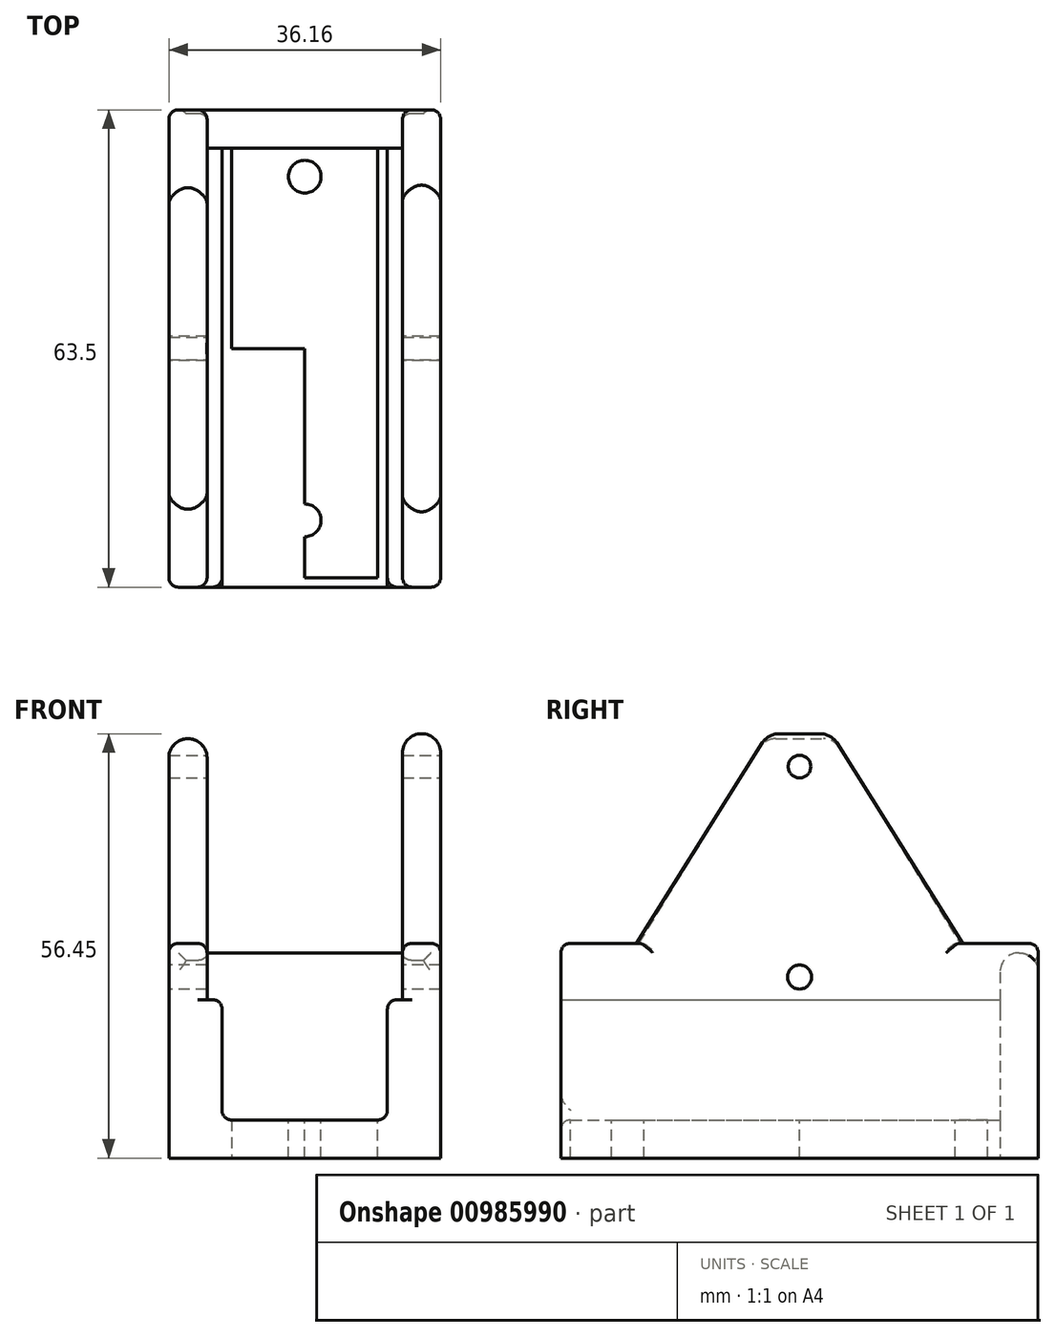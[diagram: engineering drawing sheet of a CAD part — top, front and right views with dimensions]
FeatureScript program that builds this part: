
annotation { "Feature Type Name" : "Feature", "Feature Type Description" : "" }
export const myFeature = defineFeature(function(context is Context, id is Id, definition is map)
    precondition{}
    {
        {
            var Q0;
            Q0=qCreatedBy(makeId("Front.planeOp"),FACE);
            var sketch = newSketch(context, id + "F0", { "sketchPlane" : qUnion([Q0])});
            skLineSegment(sketch, "E0", {"start": v(0, 0) * mm, "end": v(0, 23.5) * mm});
            skLineSegment(sketch, "E1", {"start": v(0, 0) * mm, "end": v(26, 0) * mm});
            skLineSegment(sketch, "E2", {"start": v(26, 0) * mm, "end": v(26, 23.5) * mm});
            skLineSegment(sketch, "E3.0", {"start": v(31.08, -5.08) * mm, "end": v(31.08, 23.5) * mm});
            skLineSegment(sketch, "E3.1", {"start": v(-5.08, -5.08) * mm, "end": v(31.08, -5.08) * mm});
            skLineSegment(sketch, "E3.2", {"start": v(-5.08, -5.08) * mm, "end": v(-5.08, 23.5) * mm});
            skLineSegment(sketch, "E4", {"start": v(-5.08, 23.5) * mm, "end": v(0, 23.5) * mm});
            skLineSegment(sketch, "E5", {"start": v(26, 23.5) * mm, "end": v(31.08, 23.5) * mm});
            skPoint(sketch, "E6.visualSharp", {"position": v(26, 0) * mm});
            skLineSegment(sketch, "E6.filletArc", {"start": v(26, 0) * mm, "end": v(26, 0) * mm});
            skPoint(sketch, "E7.visualSharp", {"position": v(0, 0) * mm});
            skLineSegment(sketch, "E7.filletArc", {"start": v(0, 0) * mm, "end": v(0, 0) * mm});
            skLineSegment(sketch, "E8.bottom", {"start": v(0, 0) * mm, "end": v(2, 0) * mm});
            skLineSegment(sketch, "E8.top", {"start": v(0, 16) * mm, "end": v(2, 16) * mm});
            skLineSegment(sketch, "E8.left", {"start": v(0, 0) * mm, "end": v(0, 16) * mm});
            skLineSegment(sketch, "E8.right", {"start": v(2, 0) * mm, "end": v(2, 16) * mm});
            skLineSegment(sketch, "E9.MirrorCS", {"start": v(24, 0) * mm, "end": v(24, 16) * mm});
            skLineSegment(sketch, "E10.MirrorCS", {"start": v(26, 16) * mm, "end": v(24, 16) * mm});
            skLineSegment(sketch, "E11.MirrorCS", {"start": v(26, 0) * mm, "end": v(26, 16) * mm});
            skLineSegment(sketch, "E12.MirrorCS", {"start": v(26, 0) * mm, "end": v(24, 0) * mm});
            skLineSegment(sketch, "E13", {"start": v(24, 0) * mm, "end": v(30.18, 0) * mm});
            skPoint(sketch, "E13.endSnap0", {"position": v(25, 0) * mm});
            skSolve(sketch);
        }
        {
            var Q0;
            Q0 = qSketchRegion(id + "F0", true);
            var Q1;
            Q1=sQuery(id+"F0.wireOp",EDGE,"E1");
            extrude(context, id + "F1", {"entities" : qUnion([Q0]), "surfaceEntities" : qUnion([Q1]), "endBound" : BoundingType.SYMMETRIC, "depth" : 63.5 * mm, "offsetDistance" : 25.4 * mm});
        }
        {
            var Q0;
            Q0=makeQuery(id+"F1.opExtrude","SWEPT_FACE",FACE,{"disambiguationData":[OSD([sQuery(id+"F0.wireOp",EDGE,"E3.2")])]});
            var sketch = newSketch(context, id + "F2", { "sketchPlane" : qUnion([Q0])});
            skCircle(sketch, "E14", {"center": v(0, 19) * mm, "radius": 1.6 * mm});
            skLineSegment(sketch, "E15", {"start": v(0, 0) * mm, "end": v(0, 23.5) * mm, "construction": true});
            skLineSegment(sketch, "E16", {"start": v(-31.75, 19) * mm, "end": v(31.75, 19) * mm, "construction": true});
            skLineSegment(sketch, "E17", {"start": v(31.75, 0) * mm, "end": v(-31.75, 0) * mm, "construction": true});
            skLineSegment(sketch, "E18", {"start": v(0, 12.26) * mm, "end": v(-31.75, 12.26) * mm, "construction": true});
            skLineSegment(sketch, "E19", {"start": v(0, 8.67) * mm, "end": v(31.75, 8.67) * mm, "construction": true});
            skLineSegment(sketch, "E20", {"start": v(-6.34, 0) * mm, "end": v(-6.34, 19) * mm, "construction": true});
            skSolve(sketch);
        }
        {
            var Q0;
            Q0 = qSketchRegion(id + "F2", true);
            extrude(context, id + "F3", {"entities" : qUnion([Q0]), "operationType" : NewBodyOperationType.REMOVE, "endBound" : BoundingType.THROUGH_ALL, "oppositeDirection" : true, "depth" : 25.4 * mm, "offsetDistance" : 25.4 * mm});
        }
        {
            var Q0;
            Q0=makeQuery(id+"F1.opExtrude","SWEPT_EDGE",EDGE,{"disambiguationData":[OSD([sQuery(id+"F0.wireOp",EDGE,"E9.MirrorCS"),sQuery(id+"F0.wireOp",EDGE,"E10.MirrorCS")])]});
            var Q1;
            Q1=makeQuery(id+"F1.opExtrude","SWEPT_EDGE",EDGE,{"disambiguationData":[OSD([sQuery(id+"F0.wireOp",EDGE,"E8.top"),sQuery(id+"F0.wireOp",EDGE,"E8.right")])]});
            var Q2;
            Q2=makeQuery(id+"F1.opExtrude","SWEPT_EDGE",EDGE,{"disambiguationData":[OSD([sQuery(id+"F0.wireOp",EDGE,"E2"),sQuery(id+"F0.wireOp",EDGE,"E5")])]});
            var Q3;
            Q3=makeQuery(id+"F1.opExtrude","SWEPT_EDGE",EDGE,{"disambiguationData":[OSD([sQuery(id+"F0.wireOp",EDGE,"E3.0"),sQuery(id+"F0.wireOp",EDGE,"E5")])]});
            var Q4;
            Q4=makeQuery(id+"F1.opExtrude","SWEPT_EDGE",EDGE,{"disambiguationData":[OSD([sQuery(id+"F0.wireOp",EDGE,"E0"),sQuery(id+"F0.wireOp",EDGE,"E4")])]});
            var Q5;
            Q5=makeQuery(id+"F1.opExtrude","SWEPT_EDGE",EDGE,{"disambiguationData":[OSD([sQuery(id+"F0.wireOp",EDGE,"E3.2"),sQuery(id+"F0.wireOp",EDGE,"E4")])]});
            var Q6;
            Q6=makeQuery(id+"F1.opExtrude","SWEPT_EDGE",EDGE,{"disambiguationData":[OSD([sQuery(id+"F0.wireOp",EDGE,"E1"),sQuery(id+"F0.wireOp",EDGE,"E9.MirrorCS"),sQuery(id+"F0.wireOp",EDGE,"E13")])]});
            var Q7;
            Q7=makeQuery(id+"F1.opExtrude","SWEPT_EDGE",EDGE,{"disambiguationData":[OSD([sQuery(id+"F0.wireOp",EDGE,"E1"),sQuery(id+"F0.wireOp",EDGE,"E8.bottom"),sQuery(id+"F0.wireOp",EDGE,"E8.right")])]});
            var Q8;
            Q8=makeQuery(id+"F1.opExtrude","CAP_EDGE",EDGE,{"disambiguationData":[OSD([sQuery(id+"F0.wireOp",EDGE,"E1")])],"isStart":true});
            var Q9;
            Q9=makeQuery(id+"F1.opExtrude","CAP_EDGE",EDGE,{"disambiguationData":[OSD([sQuery(id+"F0.wireOp",EDGE,"E1")])],"isStart":false});
            var Q10;
            Q10=makeQuery(id+"F1.opExtrude","CAP_EDGE",EDGE,{"disambiguationData":[OSD([sQuery(id+"F0.wireOp",EDGE,"E0")])],"isStart":false});
            var Q11;
            Q11=makeQuery(id+"F1.opExtrude","CAP_EDGE",EDGE,{"disambiguationData":[OSD([sQuery(id+"F0.wireOp",EDGE,"E2")])],"isStart":false});
            var Q12;
            Q12=makeQuery(id+"F1.opExtrude","CAP_EDGE",EDGE,{"disambiguationData":[OSD([sQuery(id+"F0.wireOp",EDGE,"E2")])],"isStart":true});
            var Q13;
            Q13=makeQuery(id+"F1.opExtrude","CAP_EDGE",EDGE,{"disambiguationData":[OSD([sQuery(id+"F0.wireOp",EDGE,"E0")])],"isStart":true});
            var Q14;
            Q14=makeQuery(id+"F1.opExtrude","CAP_EDGE",EDGE,{"disambiguationData":[OSD([sQuery(id+"F0.wireOp",EDGE,"E3.0")])],"isStart":true});
            var Q15;
            Q15=makeQuery(id+"F1.opExtrude","CAP_EDGE",EDGE,{"disambiguationData":[OSD([sQuery(id+"F0.wireOp",EDGE,"E3.2")])],"isStart":true});
            var Q16;
            Q16=makeQuery(id+"F1.opExtrude","CAP_EDGE",EDGE,{"disambiguationData":[OSD([sQuery(id+"F0.wireOp",EDGE,"E3.2")])],"isStart":false});
            var Q17;
            Q17=makeQuery(id+"F1.opExtrude","CAP_EDGE",EDGE,{"disambiguationData":[OSD([sQuery(id+"F0.wireOp",EDGE,"E3.0")])],"isStart":false});
            var Q18;
            Q18=makeQuery(id+"F1.opExtrude","CAP_EDGE",EDGE,{"disambiguationData":[OSD([sQuery(id+"F0.wireOp",EDGE,"E4")])],"isStart":false});
            var Q19;
            Q19=makeQuery(id+"F1.opExtrude","CAP_EDGE",EDGE,{"disambiguationData":[OSD([sQuery(id+"F0.wireOp",EDGE,"E5")])],"isStart":false});
            var Q20;
            Q20=makeQuery(id+"F1.opExtrude","CAP_EDGE",EDGE,{"disambiguationData":[OSD([sQuery(id+"F0.wireOp",EDGE,"E4")])],"isStart":true});
            var Q21;
            Q21=makeQuery(id+"F1.opExtrude","CAP_EDGE",EDGE,{"disambiguationData":[OSD([sQuery(id+"F0.wireOp",EDGE,"E5")])],"isStart":true});
            fillet(context, id + "F4", {"entities" : qUnion([Q0, Q1, Q2, Q3, Q4, Q5, Q6, Q7, Q8, Q9, Q10, Q11, Q12, Q13, Q14, Q15, Q16, Q17, Q18, Q19, Q20, Q21]), "tangentPropagation" : true, "radius" : 1.27 * mm, "defaultsChanged" : false, "vertexSettings" : [], "allowEdgeOverflow" : false});
        }
        {
            var Q0;
            Q0=makeQuery(id+"F1.opExtrude","SWEPT_FACE",FACE,{"disambiguationData":[OSD([sQuery(id+"F0.wireOp",EDGE,"E3.0")])]});
            var sketch = newSketch(context, id + "F5", { "sketchPlane" : qUnion([Q0])});
            skLineSegment(sketch, "E21", {"start": v(-22.52, 22.23) * mm, "end": v(-4.93, 50.18) * mm});
            skLineSegment(sketch, "E22.MirrorCS", {"start": v(22.52, 22.23) * mm, "end": v(4.93, 50.18) * mm});
            skLineSegment(sketch, "E23", {"start": v(-2.78, 51.37) * mm, "end": v(2.78, 51.37) * mm});
            skLineSegment(sketch, "E24", {"start": v(-22.52, 22.23) * mm, "end": v(22.52, 22.23) * mm});
            skPoint(sketch, "E25.visualSharp", {"position": v(-4.18, 51.37) * mm});
            skArc(sketch, "E25.filletArc", {"start": v(-2.78, 51.37) * mm, "mid": v(-4, 51.05) * mm, "end": v(-4.93, 50.18) * mm});
            skPoint(sketch, "E26.visualSharp", {"position": v(4.18, 51.37) * mm});
            skArc(sketch, "E26.filletArc", {"start": v(4.93, 50.18) * mm, "mid": v(4, 51.05) * mm, "end": v(2.78, 51.37) * mm});
            skSolve(sketch);
        }
        {
            var Q0;
            Q0=makeQuery(id+"F5.imprint","IMPRINT",FACE,{"disambiguationData":[TD([[makeQuery(id+"F5.imprint","IMPRINT",EDGE,{"derivedFrom":sQuery(id+"F5.wireOp",EDGE,"E21")}),-1.0]])]});
            extrude(context, id + "F6", {"entities" : qUnion([Q0]), "operationType" : NewBodyOperationType.ADD, "oppositeDirection" : true, "depth" : 5.08 * mm, "offsetDistance" : 25.4 * mm});
        }
        {
            var Q0;
            Q0=makeQuery(id+"F1.opExtrude","SWEPT_FACE",FACE,{"disambiguationData":[OSD([sQuery(id+"F0.wireOp",EDGE,"E3.2")])]});
            var sketch = newSketch(context, id + "F7", { "sketchPlane" : qUnion([Q0])});
            skLineSegment(sketch, "E27", {"start": v(-22.17, 22.22) * mm, "end": v(-4.57, 50.71) * mm});
            skLineSegment(sketch, "E28.MirrorCS", {"start": v(22.17, 22.22) * mm, "end": v(4.57, 50.71) * mm});
            skLineSegment(sketch, "E29", {"start": v(-4.57, 50.71) * mm, "end": v(4.57, 50.71) * mm});
            skLineSegment(sketch, "E30", {"start": v(-22.17, 22.23) * mm, "end": v(22.17, 22.22) * mm});
            skSolve(sketch);
        }
        {
            var Q0;
            Q0=makeQuery(id+"F7.imprint","IMPRINT",FACE,{"disambiguationData":[TD([[makeQuery(id+"F7.imprint","IMPRINT",EDGE,{"derivedFrom":sQuery(id+"F7.wireOp",EDGE,"E27")}),-1.0]])]});
            extrude(context, id + "F8", {"entities" : qUnion([Q0]), "operationType" : NewBodyOperationType.ADD, "oppositeDirection" : true, "depth" : 5.08 * mm, "offsetDistance" : 25.4 * mm});
        }
        {
            var Q0;
            Q0=makeQuery(id+"F8.opExtrude","SWEPT_EDGE",EDGE,{"disambiguationData":[OSD([sQuery(id+"F7.wireOp",EDGE,"E27"),sQuery(id+"F7.wireOp",EDGE,"E29")])]});
            var Q1;
            Q1=makeQuery(id+"F8.opExtrude","SWEPT_EDGE",EDGE,{"disambiguationData":[OSD([sQuery(id+"F7.wireOp",EDGE,"E28.MirrorCS"),sQuery(id+"F7.wireOp",EDGE,"E29")])]});
            var Q2;
            Q2=makeQuery(id+"F8.opExtrude","CAP_EDGE",EDGE,{"disambiguationData":[OSD([sQuery(id+"F7.wireOp",EDGE,"E28.MirrorCS")])],"isStart":false});
            var Q3;
            Q3=makeQuery(id+"F8.opExtrude","CAP_EDGE",EDGE,{"disambiguationData":[OSD([sQuery(id+"F7.wireOp",EDGE,"E28.MirrorCS")])],"isStart":true});
            var Q4;
            Q4=makeQuery(id+"F8.opExtrude","CAP_EDGE",EDGE,{"disambiguationData":[OSD([sQuery(id+"F7.wireOp",EDGE,"E27")])],"isStart":true});
            var Q5;
            Q5=makeQuery(id+"F8.opExtrude","CAP_EDGE",EDGE,{"disambiguationData":[OSD([sQuery(id+"F7.wireOp",EDGE,"E27")])],"isStart":false});
            var Q6;
            Q6=makeQuery(id+"F6.opExtrude","CAP_EDGE",EDGE,{"disambiguationData":[OSD([sQuery(id+"F5.wireOp",EDGE,"E22.MirrorCS")])],"isStart":false});
            var Q7;
            Q7=makeQuery(id+"F6.opExtrude","CAP_EDGE",EDGE,{"disambiguationData":[OSD([sQuery(id+"F5.wireOp",EDGE,"E22.MirrorCS")])],"isStart":true});
            var Q8;
            Q8=makeQuery(id+"F8.opExtrude","SWEPT_FACE",FACE,{"disambiguationData":[OSD([sQuery(id+"F7.wireOp",EDGE,"E29")])]});
            fillet(context, id + "F9", {"entities" : qUnion([Q0, Q1, Q2, Q3, Q4, Q5, Q6, Q7, Q8]), "tangentPropagation" : true, "radius" : 2.54 * mm, "defaultsChanged" : false, "vertexSettings" : [], "allowEdgeOverflow" : false});
        }
        {
            var Q0;
            Q0=makeQuery(id+"F1.opExtrude","SWEPT_FACE",FACE,{"disambiguationData":[OSD([sQuery(id+"F0.wireOp",EDGE,"E1")])]});
            var sketch = newSketch(context, id + "F10", { "sketchPlane" : qUnion([Q0])});
            skLineSegment(sketch, "E31", {"start": v(13, -30.48) * mm, "end": v(13, 30.48) * mm});
            skLineSegment(sketch, "E32", {"start": v(13, 0) * mm, "end": v(0, 0) * mm});
            skLineSegment(sketch, "E33", {"start": v(13, 0) * mm, "end": v(13, -30.48) * mm});
            skLineSegment(sketch, "E34", {"start": v(13, -15.24) * mm, "end": v(13, -30.48) * mm});
            skCircle(sketch, "E35", {"center": v(13, -22.86) * mm, "radius": 2.17 * mm});
            skCircle(sketch, "E36.MirrorC", {"center": v(13, 22.86) * mm, "radius": 2.17 * mm});
            skSolve(sketch);
        }
        {
            var Q0;
            {var subQ0=sQuery(id+"F10.wireOp",EDGE,"E35");var subQ1=sQuery(id+"F10.wireOp",EDGE,"E34");var subQ2=makeQuery(id+"F10.imprint","INTERSECT",VERTEX,{"disambiguationData":[OD(0.0)],"derivedFrom":[subQ1,subQ0]});Q0=makeQuery(id+"F10.imprint","IMPRINT",FACE,{"disambiguationData":[TD([[makeQuery(id+"F10.imprint","IMPRINT",EDGE,{"disambiguationData":[TD([[subQ2,-1.0]])],"derivedFrom":subQ1}),-1.0]])]});}
            var Q1;
            {var subQ0=sQuery(id+"F10.wireOp",EDGE,"E35");var subQ1=sQuery(id+"F10.wireOp",EDGE,"E34");var subQ2=makeQuery(id+"F10.imprint","INTERSECT",VERTEX,{"disambiguationData":[OD(0.0)],"derivedFrom":[subQ1,subQ0]});Q1=makeQuery(id+"F10.imprint","IMPRINT",FACE,{"disambiguationData":[TD([[makeQuery(id+"F10.imprint","IMPRINT",EDGE,{"disambiguationData":[TD([[subQ2,-1.0]])],"derivedFrom":subQ1}),1.0]])]});}
            var Q2;
            {var subQ0=sQuery(id+"F10.wireOp",EDGE,"E36.MirrorC");var subQ1=sQuery(id+"F10.wireOp",EDGE,"E31");var subQ2=makeQuery(id+"F10.imprint","INTERSECT",VERTEX,{"disambiguationData":[OD(0.0)],"derivedFrom":[subQ1,subQ0]});Q2=makeQuery(id+"F10.imprint","IMPRINT",FACE,{"disambiguationData":[TD([[makeQuery(id+"F10.imprint","IMPRINT",EDGE,{"disambiguationData":[TD([[subQ2,-1.0]])],"derivedFrom":subQ1}),-1.0]])]});}
            var Q3;
            {var subQ0=sQuery(id+"F10.wireOp",EDGE,"E36.MirrorC");var subQ1=sQuery(id+"F10.wireOp",EDGE,"E31");var subQ2=makeQuery(id+"F10.imprint","INTERSECT",VERTEX,{"disambiguationData":[OD(0.0)],"derivedFrom":[subQ1,subQ0]});Q3=makeQuery(id+"F10.imprint","IMPRINT",FACE,{"disambiguationData":[TD([[makeQuery(id+"F10.imprint","IMPRINT",EDGE,{"disambiguationData":[TD([[subQ2,-1.0]])],"derivedFrom":subQ1}),1.0]])]});}
            extrude(context, id + "F11", {"entities" : qUnion([Q0, Q1, Q2, Q3]), "operationType" : NewBodyOperationType.REMOVE, "oppositeDirection" : true, "depth" : 25.4 * mm, "offsetDistance" : 25.4 * mm});
        }
        {
            var Q0;
            Q0=makeQuery(id+"F6.boolean.opBoolean","MERGE",FACE,{"derivedFrom":[makeQuery(id+"F1.opExtrude","SWEPT_FACE",FACE,{"disambiguationData":[OSD([sQuery(id+"F0.wireOp",EDGE,"E3.0")])]}),makeQuery(id+"F6.opExtrude","CAP_FACE",FACE,{"disambiguationData":[OSD([sQuery(id+"F5.wireOp",EDGE,"E21"),sQuery(id+"F5.wireOp",EDGE,"E22.MirrorCS"),sQuery(id+"F5.wireOp",EDGE,"E23"),sQuery(id+"F5.wireOp",EDGE,"E24"),sQuery(id+"F5.wireOp",EDGE,"E25.filletArc"),sQuery(id+"F5.wireOp",EDGE,"E26.filletArc")])],"isStart":true})]});
            var sketch = newSketch(context, id + "F12", { "sketchPlane" : qUnion([Q0])});
            skLineSegment(sketch, "E37", {"start": v(0, 19) * mm, "end": v(0, 47) * mm, "construction": true});
            skCircle(sketch, "E38", {"center": v(0, 47) * mm, "radius": 1.5 * mm});
            skSolve(sketch);
        }
        {
            var Q0;
            Q0=makeQuery(id+"F12.imprint","IMPRINT",FACE,{"disambiguationData":[TD([[makeQuery(id+"F12.imprint","IMPRINT",EDGE,{"derivedFrom":sQuery(id+"F12.wireOp",EDGE,"E38")}),1.0]])]});
            extrude(context, id + "F13", {"entities" : qUnion([Q0]), "operationType" : NewBodyOperationType.REMOVE, "endBound" : BoundingType.THROUGH_ALL, "oppositeDirection" : true, "depth" : 25.4 * mm, "offsetDistance" : 25.4 * mm});
        }
        {
            var Q0;
            Q0=makeQuery(id+"F1.opExtrude","CAP_FACE",FACE,{"disambiguationData":[OSD([sQuery(id+"F0.wireOp",EDGE,"E0"),sQuery(id+"F0.wireOp",EDGE,"E1"),sQuery(id+"F0.wireOp",EDGE,"E2"),sQuery(id+"F0.wireOp",EDGE,"E3.0"),sQuery(id+"F0.wireOp",EDGE,"E3.1"),sQuery(id+"F0.wireOp",EDGE,"E3.2"),sQuery(id+"F0.wireOp",EDGE,"E4"),sQuery(id+"F0.wireOp",EDGE,"E5"),sQuery(id+"F0.wireOp",EDGE,"E8.top"),sQuery(id+"F0.wireOp",EDGE,"E8.right"),sQuery(id+"F0.wireOp",EDGE,"E9.MirrorCS"),sQuery(id+"F0.wireOp",EDGE,"E10.MirrorCS")])],"isStart":true});
            var sketch = newSketch(context, id + "F14", { "sketchPlane" : qUnion([Q0])});
            skLineSegment(sketch, "E39.bottom", {"start": v(-29.81, 22.23) * mm, "end": v(3.81, 22.23) * mm});
            skLineSegment(sketch, "E39.top", {"start": v(-29.81, -5.08) * mm, "end": v(3.81, -5.08) * mm});
            skLineSegment(sketch, "E39.left", {"start": v(-29.81, 22.23) * mm, "end": v(-29.81, -5.08) * mm});
            skLineSegment(sketch, "E39.right", {"start": v(3.81, 22.23) * mm, "end": v(3.81, -5.08) * mm});
            skSolve(sketch);
        }
        {
            var Q0;
            Q0=makeQuery(id+"F14.imprint","IMPRINT",FACE,{"disambiguationData":[TD([[makeQuery(id+"F14.imprint","IMPRINT",EDGE,{"derivedFrom":sQuery(id+"F14.wireOp",EDGE,"E39.top")}),-1.0]])]});
            var Q1;
            {var subQ3=sQuery(id+"F0.wireOp",EDGE,"E8.top");Q1=makeQuery(id+"F14.imprint","IMPRINT",FACE,{"disambiguationData":[TD([[makeQuery(id+"F14.imprint","IMPRINT",EDGE,{"derivedFrom":makeQuery(id+"F1.opExtrude","CAP_EDGE",EDGE,{"disambiguationData":[OSD([subQ3])],"isStart":true})}),-1.0]])]});}
            extrude(context, id + "F15", {"entities" : qUnion([Q0, Q1]), "operationType" : NewBodyOperationType.ADD, "oppositeDirection" : true, "depth" : 5.08 * mm, "offsetDistance" : 25.4 * mm});
        }
        {
            var Q0;
            Q0=makeQuery(id+"FhjWuzjjdZ2otRQ_1.opPattern","COPY",EDGE,{"derivedFrom":makeQuery(id+"F15.opExtrude","CAP_EDGE",EDGE,{"disambiguationData":[OSD([sQuery(id+"F14.wireOp",EDGE,"E39.bottom")])],"isStart":true}),"instanceName":"1"});
            var Q1;
            Q1=makeQuery(id+"FhjWuzjjdZ2otRQ_1.opPattern","COPY",EDGE,{"derivedFrom":makeQuery(id+"F15.opExtrude","CAP_EDGE",EDGE,{"disambiguationData":[OSD([sQuery(id+"F14.wireOp",EDGE,"E39.bottom")])],"isStart":false}),"instanceName":"1"});
            var Q2;
            Q2=makeQuery(id+"F15.opExtrude","CAP_EDGE",EDGE,{"disambiguationData":[OSD([sQuery(id+"F14.wireOp",EDGE,"E39.bottom")])],"isStart":false});
            var Q3;
            Q3=makeQuery(id+"F15.opExtrude","CAP_EDGE",EDGE,{"disambiguationData":[OSD([sQuery(id+"F14.wireOp",EDGE,"E39.bottom")])],"isStart":true});
            fillet(context, id + "F16", {"entities" : qUnion([Q0, Q1, Q2, Q3]), "tangentPropagation" : true, "radius" : 2.54 * mm, "defaultsChanged" : false, "vertexSettings" : [], "allowEdgeOverflow" : false});
        }
    });
